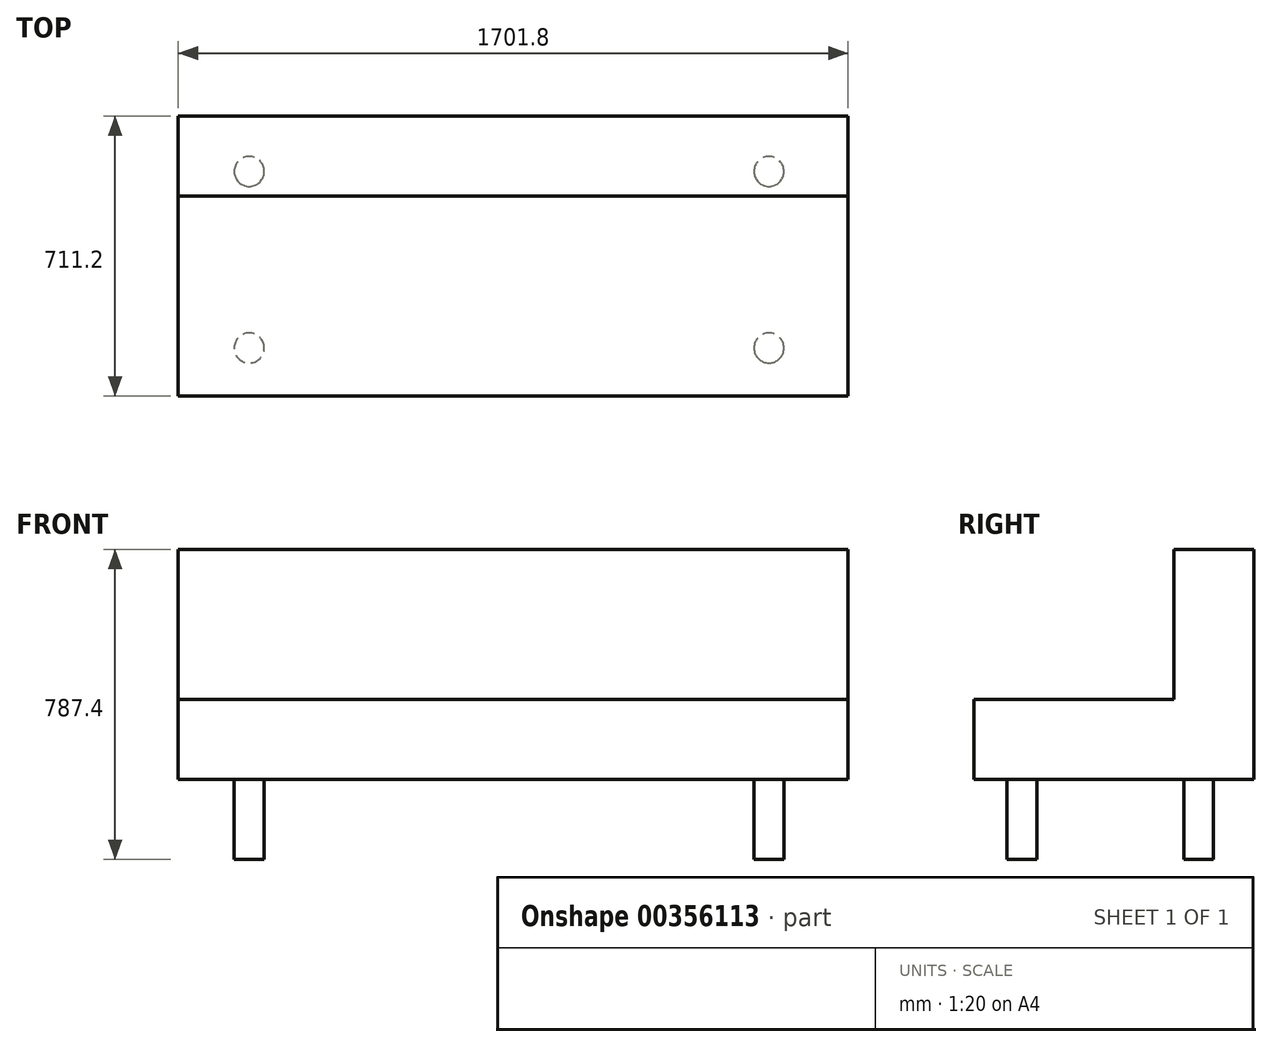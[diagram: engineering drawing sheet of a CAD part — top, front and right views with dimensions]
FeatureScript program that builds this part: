
annotation { "Feature Type Name" : "Feature", "Feature Type Description" : "" }
export const myFeature = defineFeature(function(context is Context, id is Id, definition is map)
    precondition{}
    {
        {
            var Q0;
            Q0=qCreatedBy(makeId("Right.planeOp"),FACE);
            var sketch = newSketch(context, id + "F0", { "sketchPlane" : qUnion([Q0])});
            skLineSegment(sketch, "E0.bottom", {"start": v(152.4, 292.1) * mm, "end": v(355.6, 292.1) * mm});
            skLineSegment(sketch, "E0.top", {"start": v(-355.6, -292.1) * mm, "end": v(355.6, -292.1) * mm});
            skLineSegment(sketch, "E0.left", {"start": v(-355.6, -88.9) * mm, "end": v(-355.6, -292.1) * mm});
            skLineSegment(sketch, "E0.right", {"start": v(355.6, 292.1) * mm, "end": v(355.6, -292.1) * mm});
            skPoint(sketch, "E0.middle", {"position": v(0, 0) * mm});
            skLineSegment(sketch, "E1.0", {"start": v(152.4, 292.1) * mm, "end": v(152.4, -88.9) * mm});
            skLineSegment(sketch, "E2.0", {"start": v(-355.6, -88.9) * mm, "end": v(152.4, -88.9) * mm});
            skPoint(sketch, "E3.orphan", {"position": v(-355.6, 292.1) * mm});
            skSolve(sketch);
        }
        {
            var Q0;
            Q0=makeQuery(id+"F0.imprint","IMPRINT",FACE,{"disambiguationData":[TD([[makeQuery(id+"F0.imprint","IMPRINT",EDGE,{"derivedFrom":sQuery(id+"F0.wireOp",EDGE,"E0.bottom")}),-1.0]])]});
            extrude(context, id + "F1", {"entities" : qUnion([Q0]), "endBound" : BoundingType.SYMMETRIC, "depth" : 1701.8 * mm});
        }
        {
            var Q0;
            Q0=makeQuery(id+"F1.opExtrude","SWEPT_FACE",FACE,{"disambiguationData":[OSD([sQuery(id+"F0.wireOp",EDGE,"E0.top")])]});
            var sketch = newSketch(context, id + "F2", { "sketchPlane" : qUnion([Q0])});
            skCircle(sketch, "E4", {"center": v(-670.49, 233.56) * mm, "radius": 38.1 * mm});
            skCircle(sketch, "E5", {"center": v(-670.49, -215.02) * mm, "radius": 38.1 * mm});
            skCircle(sketch, "E6", {"center": v(649.92, 233.56) * mm, "radius": 38.1 * mm});
            skCircle(sketch, "E7", {"center": v(649.92, -215.02) * mm, "radius": 38.1 * mm});
            skSolve(sketch);
        }
        {
            var Q0;
            Q0=makeQuery(id+"F2.imprint","IMPRINT",FACE,{"disambiguationData":[TD([[makeQuery(id+"F2.imprint","IMPRINT",EDGE,{"derivedFrom":sQuery(id+"F2.wireOp",EDGE,"E4")}),1.0]])]});
            var Q1;
            Q1=makeQuery(id+"F2.imprint","IMPRINT",FACE,{"disambiguationData":[TD([[makeQuery(id+"F2.imprint","IMPRINT",EDGE,{"derivedFrom":sQuery(id+"F2.wireOp",EDGE,"E5")}),1.0]])]});
            var Q2;
            Q2=makeQuery(id+"F2.imprint","IMPRINT",FACE,{"disambiguationData":[TD([[makeQuery(id+"F2.imprint","IMPRINT",EDGE,{"derivedFrom":sQuery(id+"F2.wireOp",EDGE,"E7")}),1.0]])]});
            var Q3;
            Q3=makeQuery(id+"F2.imprint","IMPRINT",FACE,{"disambiguationData":[TD([[makeQuery(id+"F2.imprint","IMPRINT",EDGE,{"derivedFrom":sQuery(id+"F2.wireOp",EDGE,"E6")}),1.0]])]});
            extrude(context, id + "F3", {"entities" : qUnion([Q0, Q1, Q2, Q3]), "operationType" : NewBodyOperationType.ADD, "depth" : 203.2 * mm});
        }
    });
